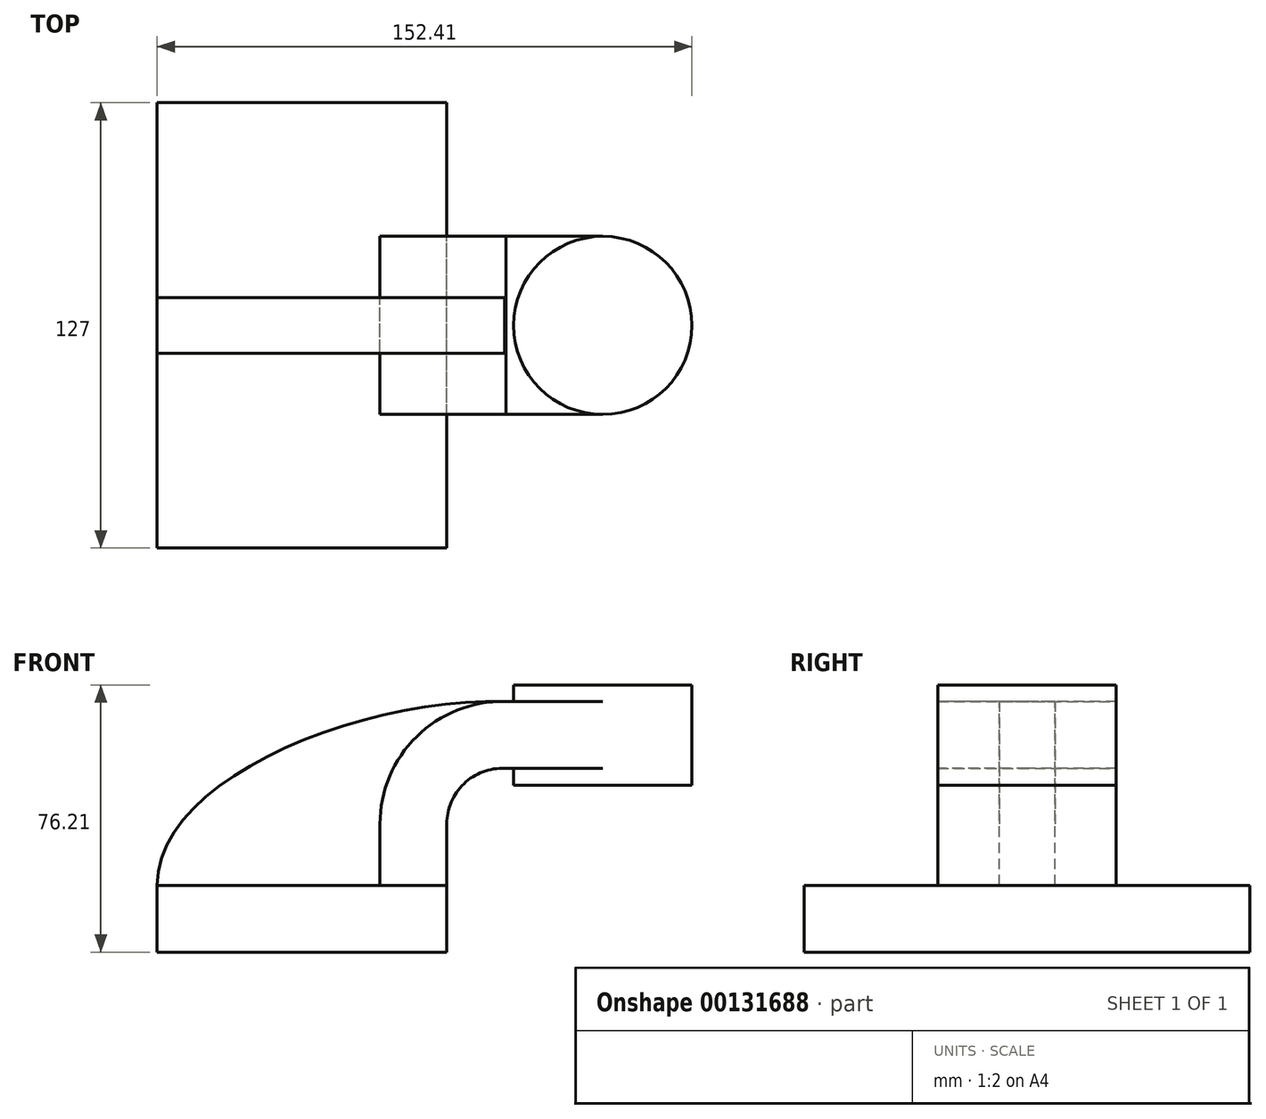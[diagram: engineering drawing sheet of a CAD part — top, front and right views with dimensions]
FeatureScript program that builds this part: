
annotation { "Feature Type Name" : "Feature", "Feature Type Description" : "" }
export const myFeature = defineFeature(function(context is Context, id is Id, definition is map)
    precondition{}
    {
        {
            var Q0;
            Q0=qCreatedBy(makeId("Front.planeOp"),FACE);
            var sketch = newSketch(context, id + "F0", { "sketchPlane" : qUnion([Q0])});
            skLineSegment(sketch, "E0.bottom", {"start": v(41.28, -9.52) * mm, "end": v(-41.28, -9.53) * mm});
            skLineSegment(sketch, "E0.top", {"start": v(41.28, 9.53) * mm, "end": v(-41.28, 9.53) * mm});
            skLineSegment(sketch, "E0.left", {"start": v(41.28, -9.52) * mm, "end": v(41.28, 9.53) * mm});
            skLineSegment(sketch, "E0.right", {"start": v(-41.28, -9.52) * mm, "end": v(-41.28, 9.53) * mm});
            skPoint(sketch, "E0.middle", {"position": v(0, 0) * mm});
            skLineSegment(sketch, "E1.bottom", {"start": v(111.12, 38.1) * mm, "end": v(60.32, 38.1) * mm});
            skLineSegment(sketch, "E1.top", {"start": v(111.12, 66.68) * mm, "end": v(60.32, 66.68) * mm});
            skLineSegment(sketch, "E1.left", {"start": v(111.12, 38.1) * mm, "end": v(111.12, 66.68) * mm});
            skLineSegment(sketch, "E1.right", {"start": v(60.32, 38.1) * mm, "end": v(60.32, 66.68) * mm});
            skPoint(sketch, "E1.middle", {"position": v(85.72, 52.39) * mm});
            skLineSegment(sketch, "E2", {"start": v(41.28, 9.53) * mm, "end": v(41.28, 27.01) * mm});
            skArc(sketch, "E3", {"start": v(41.27, 27.01) * mm, "mid": v(46.17, 38.48) * mm, "end": v(57.83, 42.88) * mm});
            skLineSegment(sketch, "E4", {"start": v(57.83, 42.88) * mm, "end": v(85.72, 42.88) * mm});
            skLineSegment(sketch, "E5.0", {"start": v(58.17, 61.93) * mm, "end": v(85.72, 61.93) * mm});
            skArc(sketch, "E5.1", {"start": v(22.23, 27.01) * mm, "mid": v(32.82, 52.07) * mm, "end": v(58.17, 61.93) * mm});
            skLineSegment(sketch, "E5.2", {"start": v(22.23, 9.53) * mm, "end": v(22.23, 27.01) * mm});
            skLineSegment(sketch, "E6", {"start": v(85.72, 38.1) * mm, "end": v(85.72, 66.68) * mm});
            skFitSpline(sketch, "E7", {"points": [v(-41.28, 9.53) * mm, v(58.17, 61.93) * mm], "startDerivative": vector(-0.53, 91.25) * mm, "endDerivative": vector(125.09, -3.22) * mm});
            skSolve(sketch);
        }
        {
            var Q0;
            Q0=makeQuery(id+"F0.imprint","IMPRINT",FACE,{"disambiguationData":[TD([[makeQuery(id+"F0.imprint","IMPRINT",EDGE,{"derivedFrom":sQuery(id+"F0.wireOp",EDGE,"E0.bottom")}),-1.0]])]});
            extrude(context, id + "F1", {"entities" : qUnion([Q0]), "endBound" : BoundingType.SYMMETRIC, "depth" : 127 * mm});
        }
        {
            var Q0;
            {var subQ1=sQuery(id+"F0.wireOp",EDGE,"E2");Q0=makeQuery(id+"F0.imprint","IMPRINT",FACE,{"disambiguationData":[TD([[makeQuery(id+"F0.imprint","IMPRINT",EDGE,{"derivedFrom":subQ1}),1.0]])]});}
            var Q1;
            {var subQ0=sQuery(id+"F0.wireOp",EDGE,"E4");var subQ1=sQuery(id+"F0.wireOp",EDGE,"E1.right");var subQ2=makeQuery(id+"F0.imprint","INTERSECT",VERTEX,{"derivedFrom":[subQ1,subQ0]});Q1=makeQuery(id+"F0.imprint","IMPRINT",FACE,{"disambiguationData":[TD([[makeQuery(id+"F0.imprint","IMPRINT",EDGE,{"disambiguationData":[TD([[subQ2,-1.0]])],"derivedFrom":subQ1}),-1.0]])]});}
            extrude(context, id + "F2", {"entities" : qUnion([Q0, Q1]), "endBound" : BoundingType.SYMMETRIC, "depth" : 50.8 * mm});
        }
        {
            var Q0;
            {var subQ3=sQuery(id+"F0.wireOp",EDGE,"E5.2");Q0=makeQuery(id+"F0.imprint","IMPRINT",FACE,{"disambiguationData":[TD([[makeQuery(id+"F0.imprint","IMPRINT",EDGE,{"derivedFrom":subQ3}),1.0]])]});}
            extrude(context, id + "F3", {"entities" : qUnion([Q0]), "endBound" : BoundingType.SYMMETRIC, "depth" : 15.88 * mm});
        }
        {
            var Q0;
            {var subQ0=sQuery(id+"F0.wireOp",EDGE,"E1.left");Q0=makeQuery(id+"F0.imprint","IMPRINT",FACE,{"disambiguationData":[TD([[makeQuery(id+"F0.imprint","IMPRINT",EDGE,{"derivedFrom":subQ0}),1.0]])]});}
            var Q1;
            Q1=sQuery(id+"F0.wireOp",EDGE,"E6");
            revolve(context, id + "F4", {"operationType" : NewBodyOperationType.ADD, "entities" : qUnion([Q0]), "axis" : qUnion([Q1]), "revolveType" : RevolveType.FULL});
        }
    });
